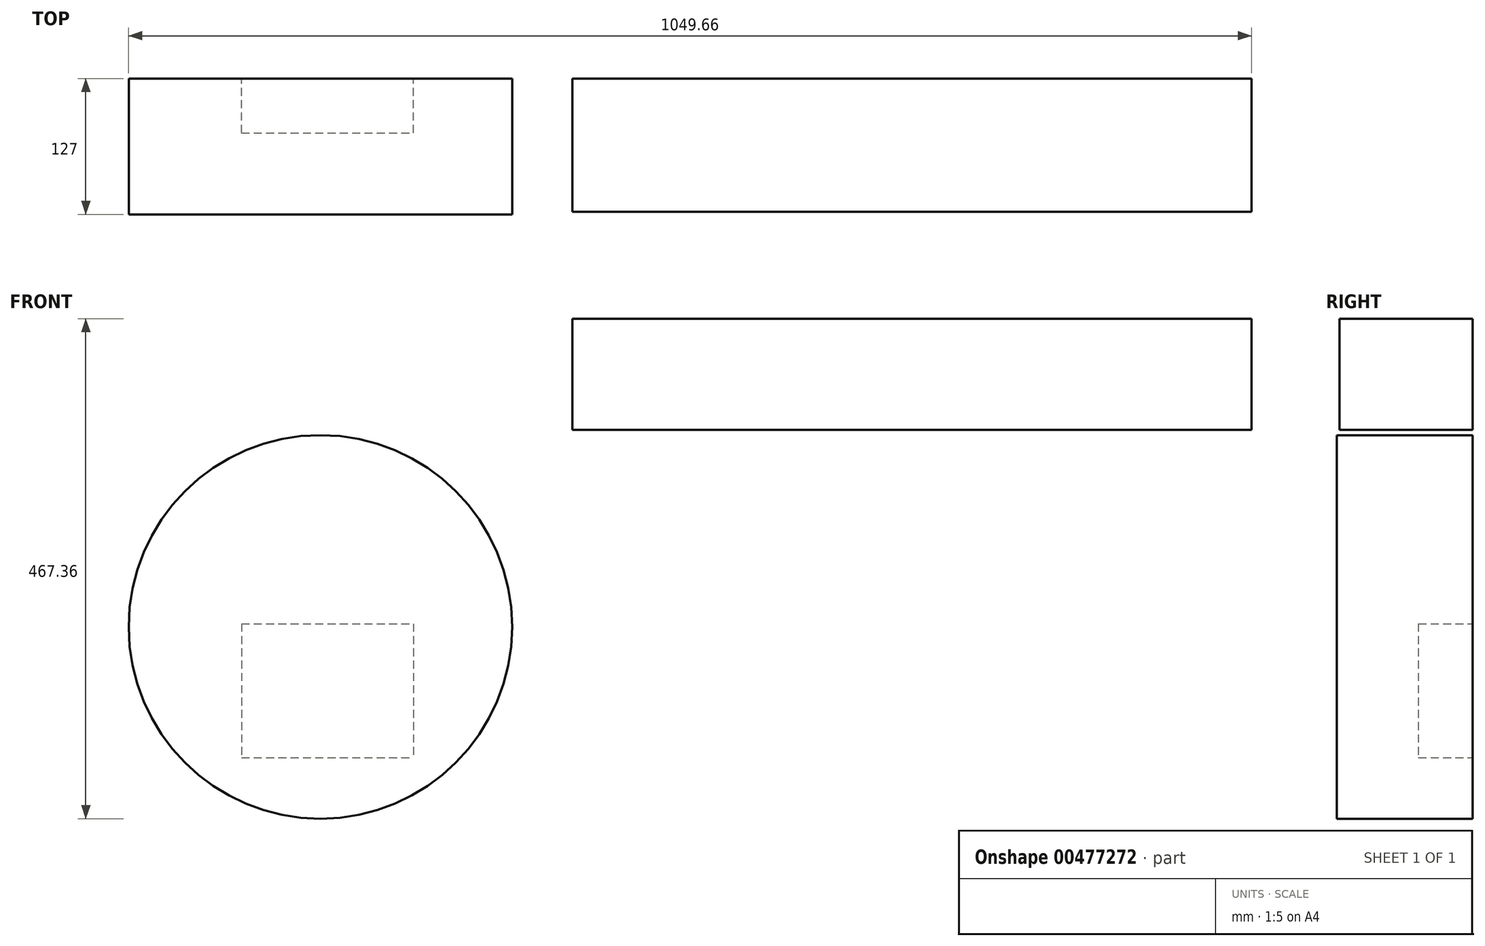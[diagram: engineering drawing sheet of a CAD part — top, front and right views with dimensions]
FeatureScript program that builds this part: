
annotation { "Feature Type Name" : "Feature", "Feature Type Description" : "" }
export const myFeature = defineFeature(function(context is Context, id is Id, definition is map)
    precondition{}
    {
        {
            var Q0;
            Q0=qCreatedBy(makeId("Right.planeOp"),FACE);
            var sketch = newSketch(context, id + "F0", { "sketchPlane" : qUnion([Q0])});
            skLineSegment(sketch, "E0.bottom", {"start": v(0, 0) * mm, "end": v(-124.6, 0) * mm});
            skLineSegment(sketch, "E0.top", {"start": v(0, 104.03) * mm, "end": v(-124.6, 104.03) * mm});
            skLineSegment(sketch, "E0.left", {"start": v(0, 0) * mm, "end": v(0, 104.03) * mm});
            skLineSegment(sketch, "E0.right", {"start": v(-124.6, 0) * mm, "end": v(-124.6, 104.03) * mm});
            skSolve(sketch);
        }
        {
            var Q0;
            Q0=makeQuery(id+"F0.imprint","IMPRINT",FACE,{"disambiguationData":[TD([[makeQuery(id+"F0.imprint","IMPRINT",EDGE,{"derivedFrom":sQuery(id+"F0.wireOp",EDGE,"E0.bottom")}),-1.0]])]});
            extrude(context, id + "F1", {"entities" : qUnion([Q0]), "depth" : 635 * mm});
        }
        {
            var Q0;
            Q0=qCreatedBy(makeId("Front.planeOp"),FACE);
            var sketch = newSketch(context, id + "F2", { "sketchPlane" : qUnion([Q0])});
            skLineSegment(sketch, "E1.bottom", {"start": v(-130.56, -64.1) * mm, "end": v(-290.34, -64.1) * mm});
            skLineSegment(sketch, "E1.top", {"start": v(-130.56, 150.7) * mm, "end": v(-290.34, 150.7) * mm});
            skLineSegment(sketch, "E1.left", {"start": v(-130.56, -64.1) * mm, "end": v(-130.56, 150.7) * mm});
            skLineSegment(sketch, "E1.right", {"start": v(-290.34, -64.1) * mm, "end": v(-290.34, 150.7) * mm});
            skSolve(sketch);
        }
        {
            var Q0;
            Q0=makeQuery(id+"F2.imprint","IMPRINT",FACE,{"disambiguationData":[TD([[makeQuery(id+"F2.imprint","IMPRINT",EDGE,{"derivedFrom":sQuery(id+"F2.wireOp",EDGE,"E1.bottom")}),-1.0]])]});
            extrude(context, id + "F3", {"entities" : qUnion([Q0]), "operationType" : NewBodyOperationType.REMOVE, "depth" : 25.4 * mm});
        }
        {
            var Q0;
            Q0=qCreatedBy(makeId("Front.planeOp"),FACE);
            var sketch = newSketch(context, id + "F4", { "sketchPlane" : qUnion([Q0])});
            skCircle(sketch, "E2", {"center": v(-235.42, -184.1) * mm, "radius": 179.24 * mm});
            skSolve(sketch);
        }
        {
            var Q0;
            Q0=makeQuery(id+"F4.imprint","IMPRINT",FACE,{"disambiguationData":[TD([[makeQuery(id+"F4.imprint","IMPRINT",EDGE,{"derivedFrom":sQuery(id+"F4.wireOp",EDGE,"E2")}),1.0]])]});
            extrude(context, id + "F5", {"entities" : qUnion([Q0]), "depth" : 127 * mm});
        }
        {
            var Q0;
            Q0=qCreatedBy(makeId("Front.planeOp"),FACE);
            var sketch = newSketch(context, id + "F6", { "sketchPlane" : qUnion([Q0])});
            skLineSegment(sketch, "E3.bottom", {"start": v(-309.24, -181.1) * mm, "end": v(-148.56, -181.1) * mm});
            skLineSegment(sketch, "E3.top", {"start": v(-309.24, -306.19) * mm, "end": v(-148.56, -306.19) * mm});
            skLineSegment(sketch, "E3.left", {"start": v(-309.24, -181.1) * mm, "end": v(-309.24, -306.19) * mm});
            skLineSegment(sketch, "E3.right", {"start": v(-148.56, -181.1) * mm, "end": v(-148.56, -306.19) * mm});
            skSolve(sketch);
        }
        {
            var Q0;
            Q0=makeQuery(id+"F6.imprint","IMPRINT",FACE,{"disambiguationData":[TD([[makeQuery(id+"F6.imprint","IMPRINT",EDGE,{"derivedFrom":sQuery(id+"F6.wireOp",EDGE,"E3.bottom")}),-1.0]])]});
            extrude(context, id + "F7", {"entities" : qUnion([Q0]), "operationType" : NewBodyOperationType.REMOVE, "depth" : 50.8 * mm});
        }
    });
